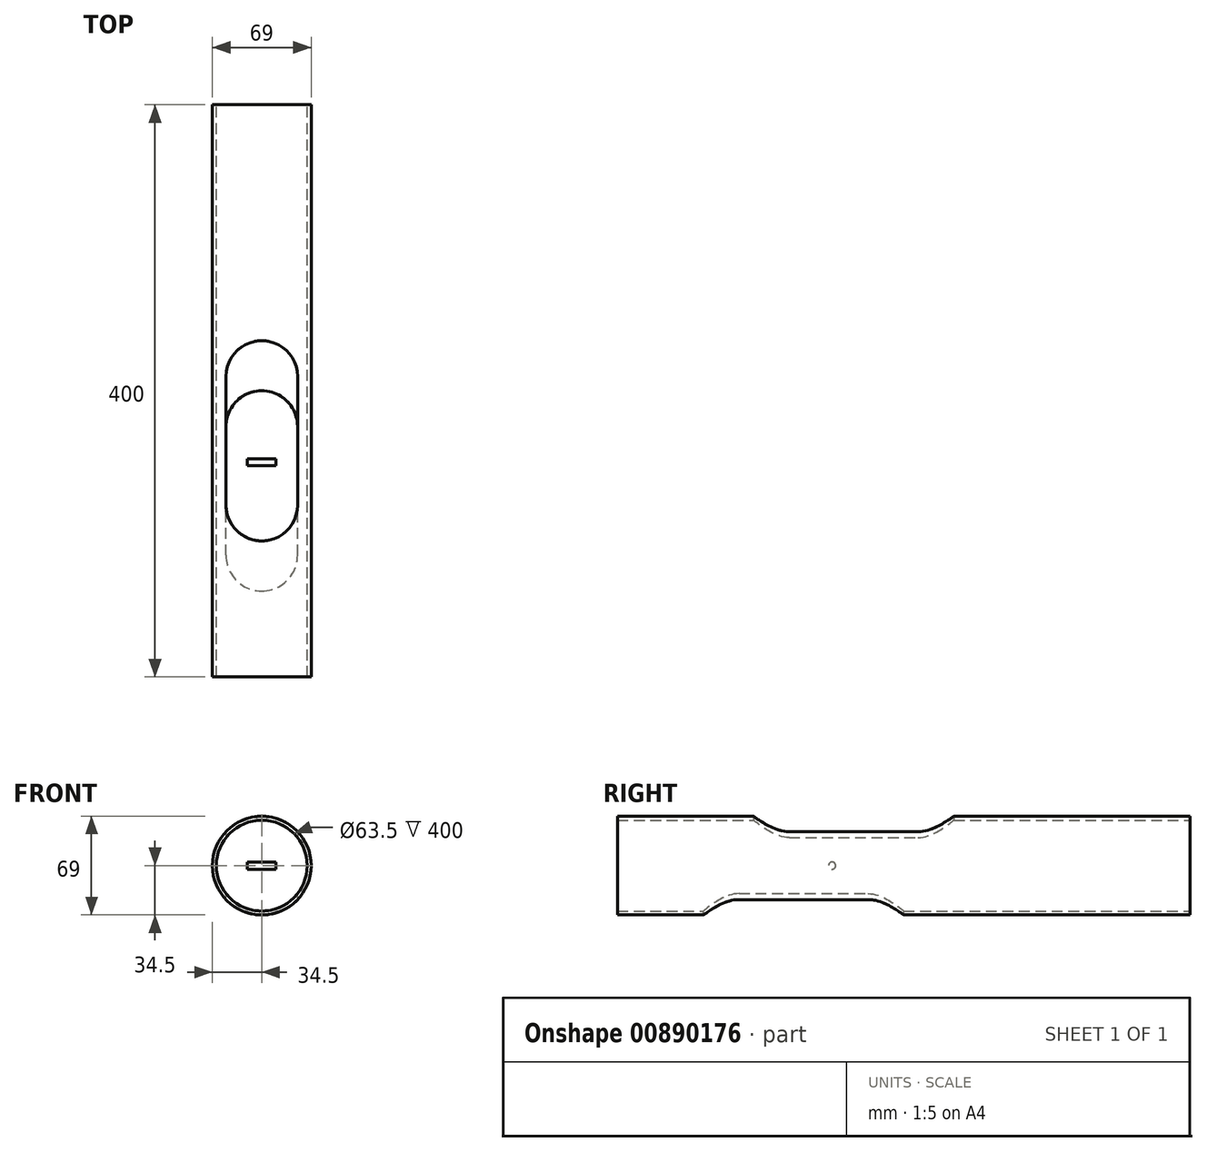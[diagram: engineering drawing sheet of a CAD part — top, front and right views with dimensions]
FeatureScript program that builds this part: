
annotation { "Feature Type Name" : "Feature", "Feature Type Description" : "" }
export const myFeature = defineFeature(function(context is Context, id is Id, definition is map)
    precondition{}
    {
        {
            var Q0;
            Q0=qCreatedBy(makeId("Front.planeOp"),FACE);
            var sketch = newSketch(context, id + "F0", { "sketchPlane" : qUnion([Q0])});
            skCircle(sketch, "E0", {"center": v(0, 0) * mm, "radius": 34.5 * mm});
            skCircle(sketch, "E1", {"center": v(0, 0) * mm, "radius": 31.75 * mm});
            skSolve(sketch);
        }
        {
            var Q0;
            Q0=qSketchRegion(id+"F0",true);
            extrude(context, id + "F1", {"entities" : qUnion([Q0]), "endBound" : BoundingType.SYMMETRIC, "depth" : 500 * mm, "offsetDistance" : 25 * mm});
        }
        {
            var Q0;
            Q0=qCreatedBy(makeId("Top.planeOp"),FACE);
            var sketch = newSketch(context, id + "F2", { "sketchPlane" : qUnion([Q0])});
            skLineSegment(sketch, "E2", {"start": v(0, 0) * mm, "end": v(0, 25) * mm});
            skLineSegment(sketch, "E3", {"start": v(0, 0) * mm, "end": v(0, -65) * mm});
            skCircle(sketch, "E4", {"center": v(0, -65) * mm, "radius": 25 * mm});
            skCircle(sketch, "E5", {"center": v(0, 25) * mm, "radius": 25 * mm});
            skLineSegment(sketch, "E6", {"start": v(-25, -65) * mm, "end": v(-25, 25) * mm});
            skLineSegment(sketch, "E7", {"start": v(25, -65) * mm, "end": v(25, 25) * mm});
            skSolve(sketch);
        }
        {
            var Q0;
            Q0=qSketchRegion(id+"F2",true);
            extrude(context, id + "F3", {"entities" : qUnion([Q0]), "operationType" : NewBodyOperationType.REMOVE, "oppositeDirection" : true, "depth" : 50 * mm, "offsetDistance" : 25 * mm});
        }
        {
            var Q0;
            Q0=qCreatedBy(makeId("Top.planeOp"),FACE);
            var sketch = newSketch(context, id + "F4", { "sketchPlane" : qUnion([Q0])});
            skLineSegment(sketch, "E8", {"start": v(0, 0) * mm, "end": v(0, 60) * mm});
            skLineSegment(sketch, "E9", {"start": v(0, 0) * mm, "end": v(0, -30) * mm});
            skCircle(sketch, "E10", {"center": v(0, -30) * mm, "radius": 25 * mm});
            skCircle(sketch, "E11", {"center": v(0, 60) * mm, "radius": 25 * mm});
            skLineSegment(sketch, "E12", {"start": v(25, -30) * mm, "end": v(25, 60) * mm});
            skLineSegment(sketch, "E13", {"start": v(-25, 60) * mm, "end": v(-25, -30) * mm});
            skSolve(sketch);
        }
        {
            var Q0;
            Q0=qSketchRegion(id+"F4",true);
            extrude(context, id + "F5", {"entities" : qUnion([Q0]), "operationType" : NewBodyOperationType.REMOVE, "depth" : 50 * mm, "offsetDistance" : 25 * mm});
        }
        {
            var Q0;
            Q0=qCreatedBy(makeId("Right.planeOp"),FACE);
            var sketch = newSketch(context, id + "F6", { "sketchPlane" : qUnion([Q0])});
            skPoint(sketch, "E14.middle", {"position": v(0, 0) * mm});
            skCircle(sketch, "E15", {"center": v(0, 0) * mm, "radius": 2.5 * mm});
            skSolve(sketch);
        }
        {
            var Q0;
            Q0=qSketchRegion(id+"F6",true);
            extrude(context, id + "F7", {"entities" : qUnion([Q0]), "endBound" : BoundingType.SYMMETRIC, "depth" : 20 * mm, "offsetDistance" : 25 * mm});
        }
        {
            var Q0;
            Q0=qCreatedBy(makeId("Right.planeOp"),FACE);
            var sketch = newSketch(context, id + "F8", { "sketchPlane" : qUnion([Q0])});
            skLineSegment(sketch, "E16", {"start": v(0, 0) * mm, "end": v(-300, 0) * mm});
            skLineSegment(sketch, "E17", {"start": v(-300, 0) * mm, "end": v(-300, 50) * mm});
            skSolve(sketch);
        }
        {
            var Q0;
            Q0=sQuery(id+"F8.wireOp",EDGE,"E17");
            var Q1;
            Q1=sQuery(id+"F8.wireOp",EDGE,"E16");
            revolve(context, id + "F9", {"bodyType" : ToolBodyType.SURFACE, "surfaceOperationType" : NewSurfaceOperationType.NEW, "surfaceEntities" : qUnion([Q0]), "axis" : qUnion([Q1]), "revolveType" : RevolveType.FULL});
        }
        {
            var Q0;
            Q0=makeQuery(id+"F9.opRevolve","SWEPT_FACE",FACE,{"disambiguationData":[OSD([sQuery(id+"F8.wireOp",EDGE,"E17")])]});
            var sketch = newSketch(context, id + "F10", { "sketchPlane" : qUnion([Q0])});
            skSolve(sketch);
        }
        {
            var Q0;
            Q0=makeQuery(id+"F10.imprint","IMPRINT",FACE,{"disambiguationData":[TD([[makeQuery(id+"F10.imprint","IMPRINT",EDGE,{"derivedFrom":makeQuery(id+"F9.opRevolve","SWEPT_EDGE",EDGE,{"disambiguationData":[OSD([sQuery(id+"F8.wireOp",VERTEX,"E17.end")])]})}),1.0]])]});
            extrude(context, id + "F11", {"entities" : qUnion([Q0]), "operationType" : NewBodyOperationType.REMOVE, "oppositeDirection" : true, "depth" : 150 * mm, "offsetDistance" : 25 * mm});
        }
    });
